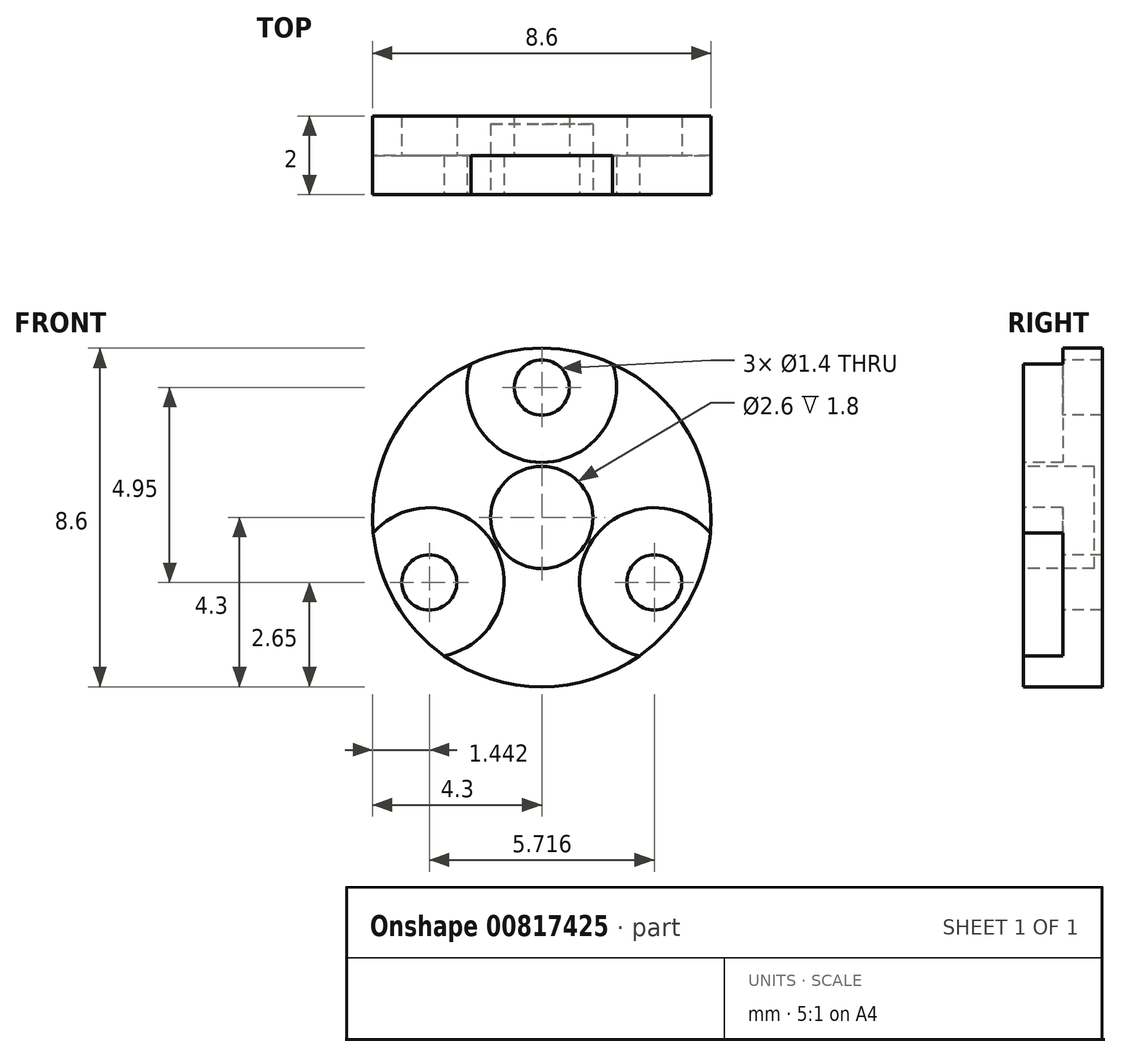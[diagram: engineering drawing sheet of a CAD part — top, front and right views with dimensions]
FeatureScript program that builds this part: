
annotation { "Feature Type Name" : "Feature", "Feature Type Description" : "" }
export const myFeature = defineFeature(function(context is Context, id is Id, definition is map)
    precondition{}
    {
        {
            var Q0;
            Q0=qCreatedBy(makeId("Front.planeOp"),FACE);
            var sketch = newSketch(context, id + "F0", { "sketchPlane" : qUnion([Q0])});
            skCircle(sketch, "E0", {"center": v(0, 0) * mm, "radius": 4.3 * mm});
            skSolve(sketch);
        }
        {
            var Q0;
            Q0=makeQuery(id+"F0.imprint","IMPRINT",FACE,{"disambiguationData":[TD([[makeQuery(id+"F0.imprint","IMPRINT",EDGE,{"derivedFrom":sQuery(id+"F0.wireOp",EDGE,"E0")}),1.0]])]});
            extrude(context, id + "F1", {"entities" : qUnion([Q0]), "depth" : 2 * mm, "offsetDistance" : 25 * mm});
        }
        {
            var Q0;
            Q0=makeQuery(id+"F1.opExtrude","CAP_FACE",FACE,{"disambiguationData":[OSD([sQuery(id+"F0.wireOp",EDGE,"E0")])],"isStart":false});
            var sketch = newSketch(context, id + "F2", { "sketchPlane" : qUnion([Q0])});
            skCircle(sketch, "E1", {"center": v(0, 3.3) * mm, "radius": 1.9 * mm});
            skCircle(sketch, "E2", {"center": v(0, 3.3) * mm, "radius": 0.7 * mm});
            skPoint(sketch, "E3.center", {"position": v(0, 0) * mm});
            skCircle(sketch, "E4.1.0", {"center": v(-2.86, -1.65) * mm, "radius": 0.7 * mm});
            skCircle(sketch, "E4.1.1", {"center": v(-2.86, -1.65) * mm, "radius": 1.9 * mm});
            skCircle(sketch, "E4.2.0", {"center": v(2.86, -1.65) * mm, "radius": 0.7 * mm});
            skCircle(sketch, "E4.2.1", {"center": v(2.86, -1.65) * mm, "radius": 1.9 * mm});
            skSolve(sketch);
        }
        {
            var Q0;
            {var subQ0=sQuery(id+"F2.wireOp",EDGE,"E1");var subQ1=makeQuery(id+"F1.opExtrude","CAP_EDGE",EDGE,{"disambiguationData":[OSD([sQuery(id+"F0.wireOp",EDGE,"E0")])],"isStart":false});var subQ2=makeQuery(id+"F2.imprint","INTERSECT",VERTEX,{"disambiguationData":[OD(0.0)],"derivedFrom":[subQ1,subQ0]});Q0=makeQuery(id+"F2.imprint","IMPRINT",FACE,{"disambiguationData":[TD([[makeQuery(id+"F2.imprint","IMPRINT",EDGE,{"disambiguationData":[TD([[subQ2,-1.0]])],"derivedFrom":subQ0}),1.0]])]});}
            var Q1;
            Q1=makeQuery(id+"F2.imprint","IMPRINT",FACE,{"disambiguationData":[TD([[makeQuery(id+"F2.imprint","IMPRINT",EDGE,{"derivedFrom":sQuery(id+"F2.wireOp",EDGE,"E4.1.0")}),-1.0]])]});
            var Q2;
            Q2=makeQuery(id+"F2.imprint","IMPRINT",FACE,{"disambiguationData":[TD([[makeQuery(id+"F2.imprint","IMPRINT",EDGE,{"derivedFrom":sQuery(id+"F2.wireOp",EDGE,"E4.2.0")}),-1.0]])]});
            extrude(context, id + "F3", {"entities" : qUnion([Q0, Q1, Q2]), "operationType" : NewBodyOperationType.REMOVE, "oppositeDirection" : true, "depth" : 1 * mm, "offsetDistance" : 25 * mm});
        }
        {
            var Q0;
            Q0=makeQuery(id+"F3.boolean.opBoolean","SPLIT",FACE,{"disambiguationData":[TD([makeQuery(id+"F3.opExtrude","SWEPT_FACE",FACE,{"disambiguationData":[OSD([sQuery(id+"F2.wireOp",EDGE,"E2")])]})])],"derivedFrom":makeQuery(id+"F1.opExtrude","CAP_FACE",FACE,{"disambiguationData":[OSD([sQuery(id+"F0.wireOp",EDGE,"E0")])],"isStart":false})});
            var Q1;
            Q1=makeQuery(id+"F3.boolean.opBoolean","SPLIT",FACE,{"disambiguationData":[TD([makeQuery(id+"F3.opExtrude","SWEPT_FACE",FACE,{"disambiguationData":[OSD([sQuery(id+"F2.wireOp",EDGE,"E4.1.0")])]})])],"derivedFrom":makeQuery(id+"F1.opExtrude","CAP_FACE",FACE,{"disambiguationData":[OSD([sQuery(id+"F0.wireOp",EDGE,"E0")])],"isStart":false})});
            var Q2;
            Q2=makeQuery(id+"F3.boolean.opBoolean","SPLIT",FACE,{"disambiguationData":[TD([makeQuery(id+"F3.opExtrude","SWEPT_FACE",FACE,{"disambiguationData":[OSD([sQuery(id+"F2.wireOp",EDGE,"E4.2.0")])]})])],"derivedFrom":makeQuery(id+"F1.opExtrude","CAP_FACE",FACE,{"disambiguationData":[OSD([sQuery(id+"F0.wireOp",EDGE,"E0")])],"isStart":false})});
            extrude(context, id + "F4", {"entities" : qUnion([Q0, Q1, Q2]), "operationType" : NewBodyOperationType.REMOVE, "oppositeDirection" : true, "depth" : 2 * mm, "offsetDistance" : 25 * mm});
        }
        {
            var Q0;
            {var subQ0=sQuery(id+"F0.wireOp",EDGE,"E0");Q0=makeQuery(id+"F3.boolean.opBoolean","SPLIT",FACE,{"disambiguationData":[TD([makeQuery(id+"F1.opExtrude","SWEPT_FACE",FACE,{"disambiguationData":[OSD([subQ0])]})])],"derivedFrom":makeQuery(id+"F1.opExtrude","CAP_FACE",FACE,{"disambiguationData":[OSD([subQ0])],"isStart":false})});}
            var sketch = newSketch(context, id + "F5", { "sketchPlane" : qUnion([Q0])});
            skCircle(sketch, "E5", {"center": v(0, 0) * mm, "radius": 1.3 * mm});
            skCircle(sketch, "E6", {"center": v(0, 0) * mm, "radius": 3 * mm});
            skSolve(sketch);
        }
        {
            var Q0;
            Q0=makeQuery(id+"F5.imprint","IMPRINT",FACE,{"disambiguationData":[TD([[makeQuery(id+"F5.imprint","IMPRINT",EDGE,{"derivedFrom":sQuery(id+"F5.wireOp",EDGE,"E5")}),1.0]])]});
            extrude(context, id + "F6", {"entities" : qUnion([Q0]), "operationType" : NewBodyOperationType.REMOVE, "oppositeDirection" : true, "depth" : 1.8 * mm, "offsetDistance" : 25 * mm});
        }
    });
